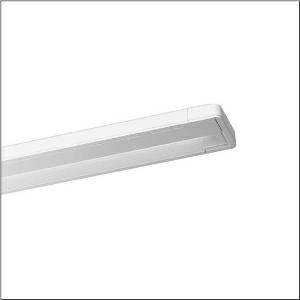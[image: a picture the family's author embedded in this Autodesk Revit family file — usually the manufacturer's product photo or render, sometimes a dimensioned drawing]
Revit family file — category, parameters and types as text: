
# Revit family: taris_r__21_5mt226d04wa_9895
name_source: partatom
category: Lighting Fixtures
units: mm (PartAtom-declared; Revit-internal decimal feet)

## family parameters
Cut with Voids When Loaded = No
Host = Face
Light Source = No
Part Type = Normal
Room Calculation Point = No
Round Connector Dimension = Use Diameter
Shared = No

## types (1)
- --- (1 x LED, 4080 lm, 28.9 W, 4000K)
    Apparent Load = 29 VA
    CIE Flux Codes = 66 91 98 100 100
    Color Rendering = 80
    Color Temperature = 4000K
    Default Elevation = 1800 mm
    Description = Taris® 21, office luminaire, primary light control with wallwasher, primary anti-glare with micro louvre, primary optical cover: axial lens, of PMMA, structured, light emission: direct distribution, primary light characteristic: asymmetric, installation type: surface-mounted, LED rated luminous flux: 4.080 lm, light colour: 840, colour temperature: 4000K, control gear: ECG DALI, with terminal, 5-pole, mains connection: 230V, AC, 50Hz, rated input power: 29W, luminaire housing, of plastic, traffic white (RAL 9016), length: 1.230 mm, width: 134 mm, height: 50mm, protection rating (complete): IP20, insulation class (complete): insulation class I (protective earthing), certification: CE, protection symbol: F, impact resistance: IK02, permissible ambient temperature for indoor applications: 0..+35°C, standard: EN 50419, packaging unit: 1 piece
    Height = 51 mm
    Lamp = 1 x LED
    Lamp Light Flux = 4080 lm
    Lamp Power = 28.9 W
    Lamp count = 1
    Length = 1233 mm
    Luminous efficacy = 141 lm/W
    Manufacturer = Siteco
    ModVariant = No
    Model = 5MT226D04WA
    Mounting Place = Ceiling
    Mounting Type = Surface mounted
    Number of Poles = 1
    OnlyDefault = Yes
    Power Factor = 1
    Product Name = Taris® 21
    Product group = office luminaire | ceiling mounted
    ProductGroupID = 302
    Protection Class = Protection class I
    Protection Degree = IP 20
    RLX_Detail_Level = 1
    RlxData = <blob elided: 41825 chars, md5=292415d4>
    Socket = socket
    Standby Power = 0 W
    System Light Flux = 4080 lm
    System Power = 29 W
    Type Comments = factory setting: luminous flux: 100 % | dim-lin: 254 | 200 mA
    Type Image = l_1004726.jpg
    URL = http://relux.com
    VarID = @adj_130107
    Voltage = 0 V
    Weight = 0.00 kg
    Width = 134 mm

## geometry (parser evidence)
native form markers: Blend x4, Sweep x11
no freeform markers — native parametric forms only
